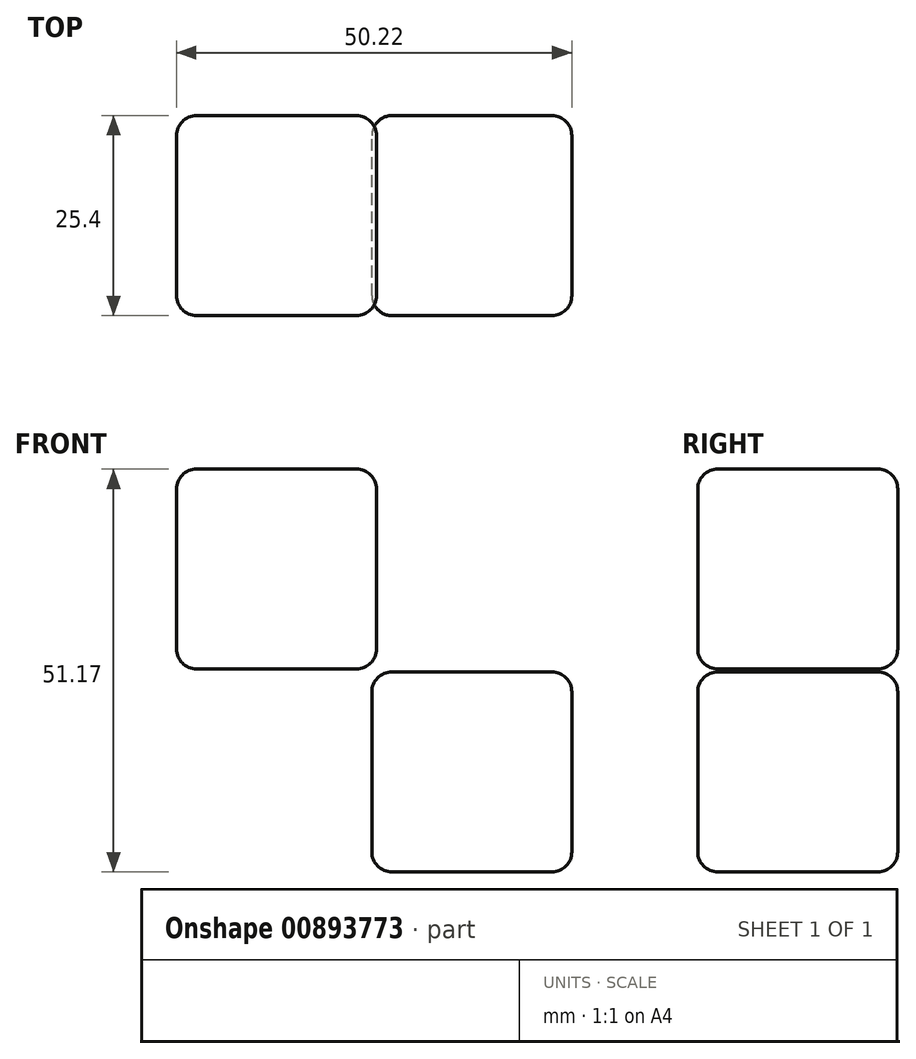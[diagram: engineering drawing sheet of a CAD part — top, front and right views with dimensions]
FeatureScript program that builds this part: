
annotation { "Feature Type Name" : "Feature", "Feature Type Description" : "" }
export const myFeature = defineFeature(function(context is Context, id is Id, definition is map)
    precondition{}
    {
        {
            var Q0;
            Q0=qCreatedBy(makeId("Front.planeOp"),FACE);
            var sketch = newSketch(context, id + "F0", { "sketchPlane" : qUnion([Q0])});
            skLineSegment(sketch, "E0.bottom", {"start": v(12.7, 12.7) * mm, "end": v(-12.7, 12.7) * mm});
            skLineSegment(sketch, "E0.top", {"start": v(12.7, -12.7) * mm, "end": v(-12.7, -12.7) * mm});
            skLineSegment(sketch, "E0.left", {"start": v(12.7, 12.7) * mm, "end": v(12.7, -12.7) * mm});
            skLineSegment(sketch, "E0.right", {"start": v(-12.7, 12.7) * mm, "end": v(-12.7, -12.7) * mm});
            skPoint(sketch, "E0.middle", {"position": v(0, 0) * mm});
            skSolve(sketch);
        }
        {
            var Q0;
            Q0=makeQuery(id+"F0.imprint","IMPRINT",FACE,{"disambiguationData":[TD([[makeQuery(id+"F0.imprint","IMPRINT",EDGE,{"derivedFrom":sQuery(id+"F0.wireOp",EDGE,"E0.bottom")}),1.0]])]});
            extrude(context, id + "F1", {"entities" : qUnion([Q0]), "depth" : 25.4 * mm, "offsetDistance" : 25.4 * mm});
        }
        {
            var Q0;
            Q0=makeQuery(id+"F1.opExtrude","SWEPT_FACE",FACE,{"disambiguationData":[OSD([sQuery(id+"F0.wireOp",EDGE,"E0.top")])]});
            var Q1;
            Q1=makeQuery(id+"F1.opExtrude","CAP_EDGE",EDGE,{"disambiguationData":[OSD([sQuery(id+"F0.wireOp",EDGE,"E0.left")])],"isStart":true});
            var Q2;
            Q2=makeQuery(id+"F1.opExtrude","CAP_FACE",FACE,{"disambiguationData":[OSD([sQuery(id+"F0.wireOp",EDGE,"E0.bottom"),sQuery(id+"F0.wireOp",EDGE,"E0.top"),sQuery(id+"F0.wireOp",EDGE,"E0.left"),sQuery(id+"F0.wireOp",EDGE,"E0.right")])],"isStart":true});
            var Q3;
            Q3=makeQuery(id+"F1.opExtrude","SWEPT_FACE",FACE,{"disambiguationData":[OSD([sQuery(id+"F0.wireOp",EDGE,"E0.left")])]});
            var Q4;
            Q4=makeQuery(id+"F1.opExtrude","SWEPT_FACE",FACE,{"disambiguationData":[OSD([sQuery(id+"F0.wireOp",EDGE,"E0.right")])]});
            var Q5;
            Q5=makeQuery(id+"F1.opExtrude","SWEPT_FACE",FACE,{"disambiguationData":[OSD([sQuery(id+"F0.wireOp",EDGE,"E0.bottom")])]});
            var Q6;
            Q6=makeQuery(id+"F1.opExtrude","CAP_FACE",FACE,{"disambiguationData":[OSD([sQuery(id+"F0.wireOp",EDGE,"E0.bottom"),sQuery(id+"F0.wireOp",EDGE,"E0.top"),sQuery(id+"F0.wireOp",EDGE,"E0.left"),sQuery(id+"F0.wireOp",EDGE,"E0.right")])],"isStart":false});
            fillet(context, id + "F2", {"entities" : qUnion([Q0, Q1, Q2, Q3, Q4, Q5, Q6]), "radius" : 2.54 * mm, "tangentPropagation" : true, "allowEdgeOverflow" : false});
        }
        {
            var Q0;
            Q0=qCreatedBy(makeId("Front.planeOp"),FACE);
            var sketch = newSketch(context, id + "F3", { "sketchPlane" : qUnion([Q0])});
            skLineSegment(sketch, "E1.bottom", {"start": v(-12.12, 13.07) * mm, "end": v(-37.52, 13.07) * mm});
            skLineSegment(sketch, "E1.top", {"start": v(-12.12, 38.47) * mm, "end": v(-37.52, 38.47) * mm});
            skLineSegment(sketch, "E1.left", {"start": v(-12.12, 13.07) * mm, "end": v(-12.12, 38.47) * mm});
            skLineSegment(sketch, "E1.right", {"start": v(-37.52, 13.07) * mm, "end": v(-37.52, 38.47) * mm});
            skSolve(sketch);
        }
        {
            var Q0;
            Q0=makeQuery(id+"F3.imprint","IMPRINT",FACE,{"disambiguationData":[TD([[makeQuery(id+"F3.imprint","IMPRINT",EDGE,{"derivedFrom":sQuery(id+"F3.wireOp",EDGE,"E1.bottom")}),-1.0]])]});
            extrude(context, id + "F4", {"entities" : qUnion([Q0]), "depth" : 25.4 * mm, "offsetDistance" : 25.4 * mm});
        }
        {
            var Q0;
            Q0=makeQuery(id+"F4.opExtrude","CAP_FACE",FACE,{"disambiguationData":[OSD([sQuery(id+"F3.wireOp",EDGE,"E1.bottom"),sQuery(id+"F3.wireOp",EDGE,"E1.top"),sQuery(id+"F3.wireOp",EDGE,"E1.left"),sQuery(id+"F3.wireOp",EDGE,"E1.right")])],"isStart":false});
            var Q1;
            Q1=makeQuery(id+"F4.opExtrude","SWEPT_FACE",FACE,{"disambiguationData":[OSD([sQuery(id+"F3.wireOp",EDGE,"E1.right")])]});
            var Q2;
            Q2=makeQuery(id+"F4.opExtrude","SWEPT_FACE",FACE,{"disambiguationData":[OSD([sQuery(id+"F3.wireOp",EDGE,"E1.bottom")])]});
            var Q3;
            Q3=makeQuery(id+"F4.opExtrude","SWEPT_FACE",FACE,{"disambiguationData":[OSD([sQuery(id+"F3.wireOp",EDGE,"E1.left")])]});
            var Q4;
            Q4=makeQuery(id+"F4.opExtrude","CAP_FACE",FACE,{"disambiguationData":[OSD([sQuery(id+"F3.wireOp",EDGE,"E1.bottom"),sQuery(id+"F3.wireOp",EDGE,"E1.top"),sQuery(id+"F3.wireOp",EDGE,"E1.left"),sQuery(id+"F3.wireOp",EDGE,"E1.right")])],"isStart":true});
            var Q5;
            Q5=makeQuery(id+"F4.opExtrude","SWEPT_FACE",FACE,{"disambiguationData":[OSD([sQuery(id+"F3.wireOp",EDGE,"E1.top")])]});
            fillet(context, id + "F5", {"entities" : qUnion([Q0, Q1, Q2, Q3, Q4, Q5]), "radius" : 2.54 * mm, "tangentPropagation" : true, "allowEdgeOverflow" : false});
        }
    });
